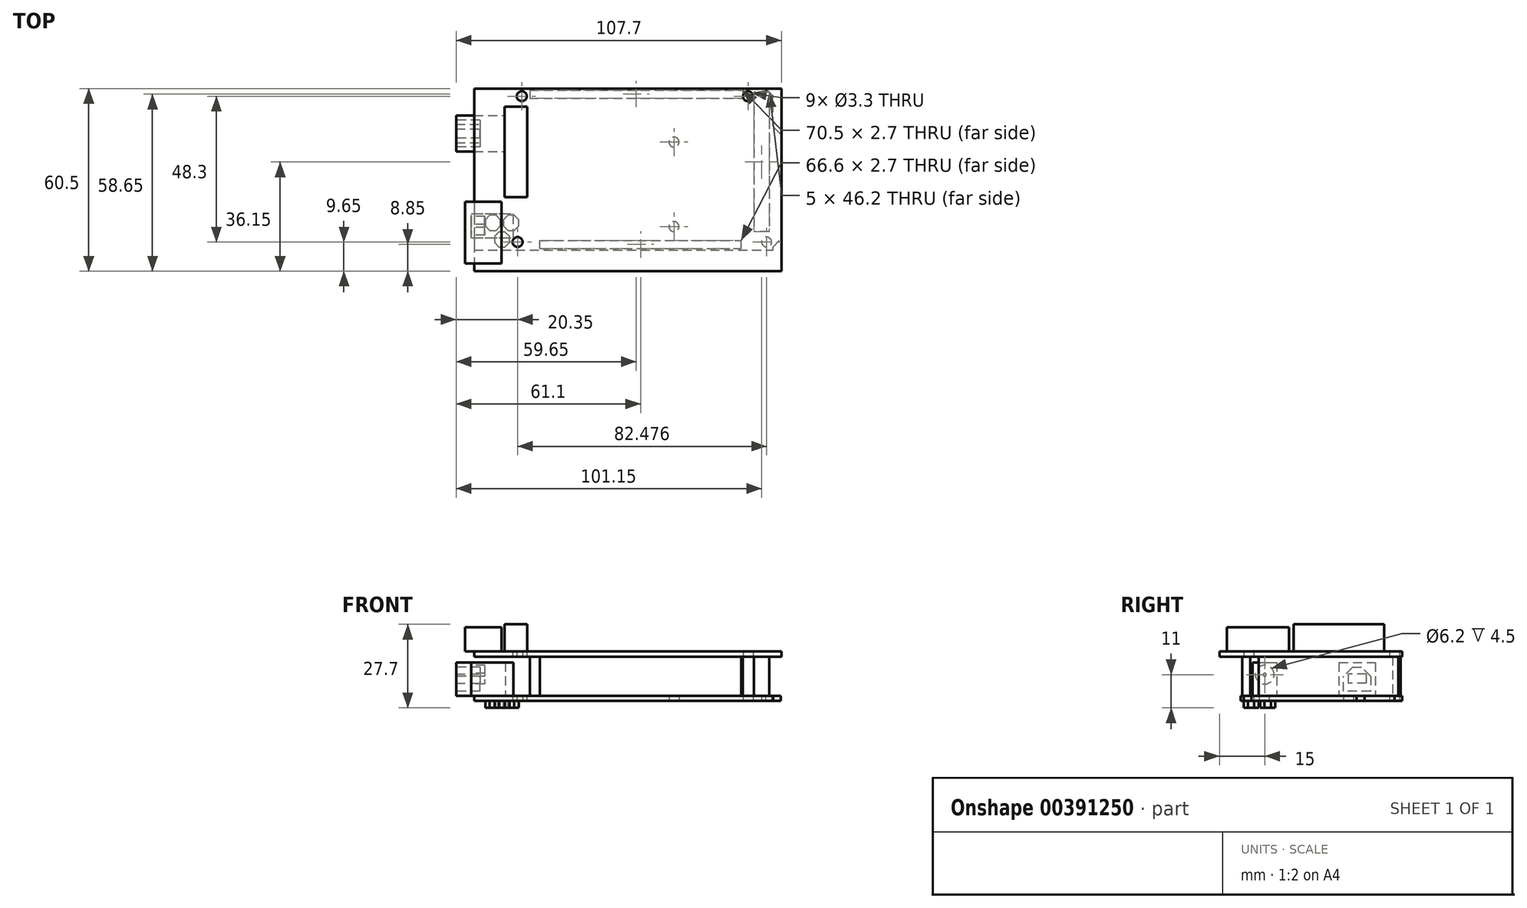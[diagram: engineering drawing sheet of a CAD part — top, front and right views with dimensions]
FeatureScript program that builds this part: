
annotation { "Feature Type Name" : "Feature", "Feature Type Description" : "" }
export const myFeature = defineFeature(function(context is Context, id is Id, definition is map)
    precondition{}
    {
        {
            var Q0;
            Q0=qCreatedBy(makeId("Top.planeOp"),FACE);
            var sketch = newSketch(context, id + "F0", { "sketchPlane" : qUnion([Q0])});
            skLineSegment(sketch, "E0.bottom", {"start": v(0, 0) * mm, "end": v(96.4, 0) * mm});
            skLineSegment(sketch, "E0.top", {"start": v(0, -53.5) * mm, "end": v(98.9, -53.5) * mm});
            skLineSegment(sketch, "E0.left", {"start": v(0, 0) * mm, "end": v(0, -53.5) * mm});
            skLineSegment(sketch, "E0.right", {"start": v(101.5, -15.1) * mm, "end": v(101.5, -49.9) * mm});
            skLineSegment(sketch, "E1", {"start": v(98.9, -53.5) * mm, "end": v(98.9, -52.5) * mm});
            skLineSegment(sketch, "E2", {"start": v(101.5, -15.1) * mm, "end": v(98.9, -12.5) * mm});
            skLineSegment(sketch, "E3", {"start": v(98.9, -52.5) * mm, "end": v(101.5, -49.9) * mm});
            skLineSegment(sketch, "E4", {"start": v(98.9, -2.5) * mm, "end": v(96.4, 0) * mm});
            skLineSegment(sketch, "E5.trimOffspring", {"start": v(98.9, -12.5) * mm, "end": v(98.9, -2.5) * mm});
            skPoint(sketch, "E6.orphan", {"position": v(98.9, 0) * mm});
            skLineSegment(sketch, "E7.bottom", {"start": v(0, -49.5) * mm, "end": v(-1, -49.5) * mm});
            skLineSegment(sketch, "E7.top", {"start": v(0, -40.5) * mm, "end": v(-1, -40.5) * mm});
            skLineSegment(sketch, "E7.left", {"start": v(0, -49.5) * mm, "end": v(0, -40.5) * mm});
            skLineSegment(sketch, "E7.right", {"start": v(-1, -49.5) * mm, "end": v(-1, -40.5) * mm});
            skLineSegment(sketch, "E8.bottom", {"start": v(0, -20.9) * mm, "end": v(-6, -20.9) * mm});
            skLineSegment(sketch, "E8.top", {"start": v(0, -8.9) * mm, "end": v(-6, -8.9) * mm});
            skLineSegment(sketch, "E8.left", {"start": v(0, -20.9) * mm, "end": v(0, -8.9) * mm});
            skLineSegment(sketch, "E8.right", {"start": v(-6, -20.9) * mm, "end": v(-6, -8.9) * mm});
            skCircle(sketch, "E9", {"center": v(15.75, -2.55) * mm, "radius": 1.65 * mm});
            skCircle(sketch, "E10", {"center": v(14.35, -50.85) * mm, "radius": 1.65 * mm});
            skCircle(sketch, "E11", {"center": v(66.15, -45.75) * mm, "radius": 1.65 * mm});
            skCircle(sketch, "E12", {"center": v(66.15, -17.75) * mm, "radius": 1.65 * mm});
            skCircle(sketch, "E13", {"center": v(96.83, -50.85) * mm, "radius": 1.65 * mm});
            skCircle(sketch, "E14", {"center": v(90.65, -2.55) * mm, "radius": 1.65 * mm});
            skLineSegment(sketch, "E15", {"start": v(15.75, -2.55) * mm, "end": v(90.65, -2.55) * mm, "construction": true});
            skLineSegment(sketch, "E16", {"start": v(14.35, -50.85) * mm, "end": v(96.83, -50.85) * mm, "construction": true});
            skLineSegment(sketch, "E17", {"start": v(66.15, -45.75) * mm, "end": v(66.15, -17.75) * mm, "construction": true});
            skSolve(sketch);
        }
        {
            var Q0;
            {var subQ3=sQuery(id+"F0.wireOp",EDGE,"E0.bottom");Q0=makeQuery(id+"F0.imprint","IMPRINT",FACE,{"disambiguationData":[TD([[makeQuery(id+"F0.imprint","IMPRINT",EDGE,{"derivedFrom":subQ3}),-1.0]])]});}
            extrude(context, id + "F1", {"entities" : qUnion([Q0]), "depth" : 1.7 * mm});
        }
        {
            var Q0;
            Q0=makeQuery(id+"F1.opExtrude","CAP_FACE",FACE,{"disambiguationData":[OSD([sQuery(id+"F0.wireOp",EDGE,"E0.bottom"),sQuery(id+"F0.wireOp",EDGE,"E0.top"),sQuery(id+"F0.wireOp",EDGE,"E0.left"),sQuery(id+"F0.wireOp",EDGE,"E0.right"),sQuery(id+"F0.wireOp",EDGE,"E1"),sQuery(id+"F0.wireOp",EDGE,"E2"),sQuery(id+"F0.wireOp",EDGE,"E3"),sQuery(id+"F0.wireOp",EDGE,"E4"),sQuery(id+"F0.wireOp",EDGE,"E5.trimOffspring"),sQuery(id+"F0.wireOp",EDGE,"E7.left"),sQuery(id+"F0.wireOp",EDGE,"E8.left"),sQuery(id+"F0.wireOp",EDGE,"E9"),sQuery(id+"F0.wireOp",EDGE,"E10"),sQuery(id+"F0.wireOp",EDGE,"E11"),sQuery(id+"F0.wireOp",EDGE,"E12"),sQuery(id+"F0.wireOp",EDGE,"E13"),sQuery(id+"F0.wireOp",EDGE,"E14")])],"isStart":true});
            var sketch = newSketch(context, id + "F2", { "sketchPlane" : qUnion([Q0])});
            skCircle(sketch, "E18.cCircle", {"center": v(9.2, 50) * mm, "radius": 2.5 * mm, "construction": true});
            skLineSegment(sketch, "E18.0", {"start": v(8.16, 52.5) * mm, "end": v(10.24, 52.5) * mm});
            skLineSegment(sketch, "E18.1", {"start": v(10.24, 52.5) * mm, "end": v(11.7, 51.04) * mm});
            skLineSegment(sketch, "E18.2", {"start": v(11.7, 51.04) * mm, "end": v(11.7, 48.96) * mm});
            skLineSegment(sketch, "E18.3", {"start": v(11.7, 48.96) * mm, "end": v(10.24, 47.5) * mm});
            skLineSegment(sketch, "E18.4", {"start": v(10.24, 47.5) * mm, "end": v(8.16, 47.5) * mm});
            skLineSegment(sketch, "E18.5", {"start": v(8.16, 47.5) * mm, "end": v(6.7, 48.96) * mm});
            skLineSegment(sketch, "E18.6", {"start": v(6.7, 48.96) * mm, "end": v(6.7, 51.04) * mm});
            skLineSegment(sketch, "E18.7", {"start": v(6.7, 51.04) * mm, "end": v(8.16, 52.5) * mm});
            skPoint(sketch, "E18.0.midPoint", {"position": v(9.2, 52.5) * mm});
            skCircle(sketch, "E19.cCircle", {"center": v(6.2, 44.51) * mm, "radius": 2.5 * mm, "construction": true});
            skLineSegment(sketch, "E19.0", {"start": v(5.16, 47.01) * mm, "end": v(7.24, 47.01) * mm});
            skLineSegment(sketch, "E19.1", {"start": v(7.24, 47.01) * mm, "end": v(8.7, 45.55) * mm});
            skLineSegment(sketch, "E19.2", {"start": v(8.7, 45.55) * mm, "end": v(8.7, 43.48) * mm});
            skLineSegment(sketch, "E19.3", {"start": v(8.7, 43.48) * mm, "end": v(7.24, 42.01) * mm});
            skLineSegment(sketch, "E19.4", {"start": v(7.24, 42.01) * mm, "end": v(5.16, 42.01) * mm});
            skLineSegment(sketch, "E19.5", {"start": v(5.16, 42.01) * mm, "end": v(3.7, 43.48) * mm});
            skLineSegment(sketch, "E19.6", {"start": v(3.7, 43.48) * mm, "end": v(3.7, 45.55) * mm});
            skLineSegment(sketch, "E19.7", {"start": v(3.7, 45.55) * mm, "end": v(5.16, 47.01) * mm});
            skPoint(sketch, "E19.0.midPoint", {"position": v(6.2, 47.01) * mm});
            skCircle(sketch, "E20.cCircle", {"center": v(12.2, 44.51) * mm, "radius": 2.5 * mm, "construction": true});
            skLineSegment(sketch, "E20.0", {"start": v(11.16, 47.01) * mm, "end": v(13.24, 47.01) * mm});
            skLineSegment(sketch, "E20.1", {"start": v(13.24, 47.01) * mm, "end": v(14.7, 45.55) * mm});
            skLineSegment(sketch, "E20.2", {"start": v(14.7, 45.55) * mm, "end": v(14.7, 43.48) * mm});
            skLineSegment(sketch, "E20.3", {"start": v(14.7, 43.48) * mm, "end": v(13.24, 42.01) * mm});
            skLineSegment(sketch, "E20.4", {"start": v(13.24, 42.01) * mm, "end": v(11.16, 42.01) * mm});
            skLineSegment(sketch, "E20.5", {"start": v(11.16, 42.01) * mm, "end": v(9.7, 43.48) * mm});
            skLineSegment(sketch, "E20.6", {"start": v(9.7, 43.48) * mm, "end": v(9.7, 45.55) * mm});
            skLineSegment(sketch, "E20.7", {"start": v(9.7, 45.55) * mm, "end": v(11.16, 47.01) * mm});
            skPoint(sketch, "E20.0.midPoint", {"position": v(12.2, 47.01) * mm});
            skSolve(sketch);
        }
        {
            var Q0;
            Q0 = qSketchRegion(id + "F2", true);
            extrude(context, id + "F3", {"entities" : qUnion([Q0]), "operationType" : NewBodyOperationType.ADD, "depth" : 2.3 * mm});
        }
        {
            var Q0;
            Q0=makeQuery(id+"F1.opExtrude","CAP_FACE",FACE,{"disambiguationData":[OSD([sQuery(id+"F0.wireOp",EDGE,"E0.bottom"),sQuery(id+"F0.wireOp",EDGE,"E0.top"),sQuery(id+"F0.wireOp",EDGE,"E0.left"),sQuery(id+"F0.wireOp",EDGE,"E0.right"),sQuery(id+"F0.wireOp",EDGE,"E1"),sQuery(id+"F0.wireOp",EDGE,"E2"),sQuery(id+"F0.wireOp",EDGE,"E3"),sQuery(id+"F0.wireOp",EDGE,"E4"),sQuery(id+"F0.wireOp",EDGE,"E5.trimOffspring"),sQuery(id+"F0.wireOp",EDGE,"E7.left"),sQuery(id+"F0.wireOp",EDGE,"E8.left"),sQuery(id+"F0.wireOp",EDGE,"E9"),sQuery(id+"F0.wireOp",EDGE,"E10"),sQuery(id+"F0.wireOp",EDGE,"E11"),sQuery(id+"F0.wireOp",EDGE,"E12"),sQuery(id+"F0.wireOp",EDGE,"E13"),sQuery(id+"F0.wireOp",EDGE,"E14")])],"isStart":false});
            var sketch = newSketch(context, id + "F4", { "sketchPlane" : qUnion([Q0])});
            skLineSegment(sketch, "E21.0.0", {"start": v(0, 0) * mm, "end": v(0, -53.5) * mm, "construction": true});
            skLineSegment(sketch, "E21.0.1", {"start": v(0, -53.5) * mm, "end": v(98.9, -53.5) * mm, "construction": true});
            skLineSegment(sketch, "E21.0.2", {"start": v(98.9, -53.5) * mm, "end": v(98.9, -52.5) * mm, "construction": true});
            skLineSegment(sketch, "E21.0.3", {"start": v(98.9, -52.5) * mm, "end": v(101.5, -49.9) * mm, "construction": true});
            skLineSegment(sketch, "E21.0.4", {"start": v(101.5, -49.9) * mm, "end": v(101.5, -15.1) * mm, "construction": true});
            skLineSegment(sketch, "E21.0.5", {"start": v(101.5, -15.1) * mm, "end": v(98.9, -12.5) * mm, "construction": true});
            skLineSegment(sketch, "E21.0.6", {"start": v(98.9, -12.5) * mm, "end": v(98.9, -2.5) * mm, "construction": true});
            skLineSegment(sketch, "E21.0.7", {"start": v(98.9, -2.5) * mm, "end": v(96.4, 0) * mm, "construction": true});
            skLineSegment(sketch, "E21.0.8", {"start": v(96.4, 0) * mm, "end": v(0, 0) * mm, "construction": true});
            skLineSegment(sketch, "E22.bottom", {"start": v(-1, -49.5) * mm, "end": v(13, -49.5) * mm});
            skLineSegment(sketch, "E22.top", {"start": v(-1, -41.5) * mm, "end": v(13, -41.5) * mm});
            skLineSegment(sketch, "E22.left", {"start": v(-1, -49.5) * mm, "end": v(-1, -41.5) * mm});
            skLineSegment(sketch, "E22.right", {"start": v(13, -49.5) * mm, "end": v(13, -41.5) * mm});
            skLineSegment(sketch, "E23.bottom", {"start": v(-6, -20.9) * mm, "end": v(10.3, -20.9) * mm});
            skLineSegment(sketch, "E23.top", {"start": v(-6, -8.9) * mm, "end": v(10.3, -8.9) * mm});
            skLineSegment(sketch, "E23.left", {"start": v(-6, -20.9) * mm, "end": v(-6, -8.9) * mm});
            skLineSegment(sketch, "E23.right", {"start": v(10.3, -20.9) * mm, "end": v(10.3, -8.9) * mm});
            skLineSegment(sketch, "E24.bottom", {"start": v(21.8, -53) * mm, "end": v(88.4, -53) * mm});
            skLineSegment(sketch, "E24.top", {"start": v(21.8, -50.3) * mm, "end": v(88.4, -50.3) * mm});
            skLineSegment(sketch, "E24.left", {"start": v(21.8, -53) * mm, "end": v(21.8, -50.3) * mm});
            skLineSegment(sketch, "E24.right", {"start": v(88.4, -53) * mm, "end": v(88.4, -50.3) * mm});
            skLineSegment(sketch, "E25.bottom", {"start": v(18.4, -0.5) * mm, "end": v(88.9, -0.5) * mm});
            skLineSegment(sketch, "E25.top", {"start": v(18.4, -3.2) * mm, "end": v(88.9, -3.2) * mm});
            skLineSegment(sketch, "E25.left", {"start": v(18.4, -0.5) * mm, "end": v(18.4, -3.2) * mm});
            skLineSegment(sketch, "E25.right", {"start": v(88.9, -0.5) * mm, "end": v(88.9, -3.2) * mm});
            skLineSegment(sketch, "E26.bottom", {"start": v(97.65, -1.25) * mm, "end": v(92.65, -1.25) * mm});
            skLineSegment(sketch, "E26.top", {"start": v(97.65, -47.45) * mm, "end": v(92.65, -47.45) * mm});
            skLineSegment(sketch, "E26.left", {"start": v(97.65, -1.25) * mm, "end": v(97.65, -47.45) * mm});
            skLineSegment(sketch, "E26.right", {"start": v(92.65, -1.25) * mm, "end": v(92.65, -47.45) * mm});
            skSolve(sketch);
        }
        {
            var Q0;
            Q0=makeQuery(id+"F4.imprint","IMPRINT",FACE,{"disambiguationData":[TD([[makeQuery(id+"F4.imprint","IMPRINT",EDGE,{"derivedFrom":sQuery(id+"F4.wireOp",EDGE,"E24.bottom")}),1.0]])]});
            var Q1;
            Q1=makeQuery(id+"F4.imprint","IMPRINT",FACE,{"disambiguationData":[TD([[makeQuery(id+"F4.imprint","IMPRINT",EDGE,{"derivedFrom":sQuery(id+"F4.wireOp",EDGE,"E25.bottom")}),-1.0]])]});
            var Q2;
            Q2=makeQuery(id+"F4.imprint","IMPRINT",FACE,{"disambiguationData":[TD([[makeQuery(id+"F4.imprint","IMPRINT",EDGE,{"derivedFrom":sQuery(id+"F4.wireOp",EDGE,"E26.bottom")}),1.0]])]});
            extrude(context, id + "F5", {"entities" : qUnion([Q0, Q1, Q2]), "operationType" : NewBodyOperationType.ADD, "depth" : 13 * mm});
        }
        {
            var Q0;
            {var subQ0=sQuery(id+"F4.wireOp",EDGE,"E23.right");Q0=makeQuery(id+"F4.imprint","IMPRINT",FACE,{"disambiguationData":[TD([[makeQuery(id+"F4.imprint","IMPRINT",EDGE,{"derivedFrom":subQ0}),1.0]])]});}
            var Q1;
            {var subQ0=sQuery(id+"F4.wireOp",EDGE,"E23.left");Q1=makeQuery(id+"F4.imprint","IMPRINT",FACE,{"disambiguationData":[TD([[makeQuery(id+"F4.imprint","IMPRINT",EDGE,{"derivedFrom":subQ0}),-1.0]])]});}
            extrude(context, id + "F6", {"entities" : qUnion([Q0, Q1]), "operationType" : NewBodyOperationType.ADD, "depth" : 11 * mm});
        }
        {
            var Q0;
            {var subQ0=sQuery(id+"F4.wireOp",EDGE,"E22.right");Q0=makeQuery(id+"F4.imprint","IMPRINT",FACE,{"disambiguationData":[TD([[makeQuery(id+"F4.imprint","IMPRINT",EDGE,{"derivedFrom":subQ0}),1.0]])]});}
            var Q1;
            {var subQ0=sQuery(id+"F4.wireOp",EDGE,"E22.left");Q1=makeQuery(id+"F4.imprint","IMPRINT",FACE,{"disambiguationData":[TD([[makeQuery(id+"F4.imprint","IMPRINT",EDGE,{"derivedFrom":subQ0}),-1.0]])]});}
            extrude(context, id + "F7", {"entities" : qUnion([Q0, Q1]), "operationType" : NewBodyOperationType.ADD, "depth" : 11 * mm});
        }
        {
            var Q0;
            Q0=makeQuery(id+"F6.opExtrude","SWEPT_FACE",FACE,{"disambiguationData":[OSD([sQuery(id+"F4.wireOp",EDGE,"E23.left")])]});
            var sketch = newSketch(context, id + "F8", { "sketchPlane" : qUnion([Q0])});
            skLineSegment(sketch, "E27.0", {"start": v(10.4, 3.2) * mm, "end": v(19.4, 3.2) * mm});
            skLineSegment(sketch, "E27.1", {"start": v(10.4, 11.2) * mm, "end": v(10.4, 3.2) * mm});
            skLineSegment(sketch, "E27.2", {"start": v(19.4, 11.2) * mm, "end": v(10.4, 11.2) * mm});
            skLineSegment(sketch, "E27.3", {"start": v(19.4, 3.2) * mm, "end": v(19.4, 11.2) * mm});
            skSolve(sketch);
        }
        {
            var Q0;
            Q0=makeQuery(id+"F8.imprint","IMPRINT",FACE,{"disambiguationData":[TD([[makeQuery(id+"F8.imprint","IMPRINT",EDGE,{"derivedFrom":sQuery(id+"F8.wireOp",EDGE,"E27.0")}),1.0]])]});
            extrude(context, id + "F9", {"entities" : qUnion([Q0]), "operationType" : NewBodyOperationType.REMOVE, "oppositeDirection" : true, "depth" : 7.9 * mm});
        }
        {
            var Q0;
            Q0=makeQuery(id+"F7.opExtrude","SWEPT_FACE",FACE,{"disambiguationData":[OSD([sQuery(id+"F4.wireOp",EDGE,"E22.left")])]});
            var sketch = newSketch(context, id + "F10", { "sketchPlane" : qUnion([Q0])});
            skCircle(sketch, "E28", {"center": v(45.5, 8.7) * mm, "radius": 3.1 * mm});
            skLineSegment(sketch, "E29", {"start": v(42.4, 8.7) * mm, "end": v(41.5, 8.7) * mm, "construction": true});
            skLineSegment(sketch, "E30", {"start": v(48.6, 8.7) * mm, "end": v(49.5, 8.7) * mm, "construction": true});
            skLineSegment(sketch, "E31", {"start": v(45.5, 11.8) * mm, "end": v(45.5, 12.7) * mm, "construction": true});
            skCircle(sketch, "E32", {"center": v(45.5, 8.7) * mm, "radius": 0.5 * mm});
            skSolve(sketch);
        }
        {
            var Q0;
            Q0 = qSketchRegion(id + "F10", true);
            extrude(context, id + "F11", {"entities" : qUnion([Q0]), "operationType" : NewBodyOperationType.REMOVE, "oppositeDirection" : true, "depth" : 4.5 * mm});
        }
        {
            var Q0;
            Q0=makeQuery(id+"F9.boolean.opBoolean","COPY",EDGE,{"derivedFrom":makeQuery(id+"F9.opExtrude","SWEPT_EDGE",EDGE,{"disambiguationData":[OSD([sQuery(id+"F8.wireOp",EDGE,"E27.1"),sQuery(id+"F8.wireOp",EDGE,"E27.2")])]})});
            var Q1;
            Q1=makeQuery(id+"F9.boolean.opBoolean","COPY",EDGE,{"derivedFrom":makeQuery(id+"F9.opExtrude","SWEPT_EDGE",EDGE,{"disambiguationData":[OSD([sQuery(id+"F8.wireOp",EDGE,"E27.2"),sQuery(id+"F8.wireOp",EDGE,"E27.3")])]})});
            chamfer(context, id + "F12", {"entities" : qUnion([Q0, Q1]), "width" : 3 * mm, "tangentPropagation" : true});
        }
        {
            var Q0;
            Q0=makeQuery(id+"F9.boolean.opBoolean","COPY",FACE,{"derivedFrom":makeQuery(id+"F9.opExtrude","CAP_FACE",FACE,{"disambiguationData":[OSD([sQuery(id+"F8.wireOp",EDGE,"E27.0"),sQuery(id+"F8.wireOp",EDGE,"E27.1"),sQuery(id+"F8.wireOp",EDGE,"E27.2"),sQuery(id+"F8.wireOp",EDGE,"E27.3")])],"isStart":false})});
            var sketch = newSketch(context, id + "F13", { "sketchPlane" : qUnion([Q0])});
            skLineSegment(sketch, "E33.bottom", {"start": v(11.9, 8.9) * mm, "end": v(17.9, 8.9) * mm});
            skLineSegment(sketch, "E33.top", {"start": v(11.9, 5.9) * mm, "end": v(17.9, 5.9) * mm});
            skLineSegment(sketch, "E33.left", {"start": v(11.9, 8.9) * mm, "end": v(11.9, 5.9) * mm});
            skLineSegment(sketch, "E33.right", {"start": v(17.9, 8.9) * mm, "end": v(17.9, 5.9) * mm});
            skLineSegment(sketch, "E34", {"start": v(11.9, 6.28) * mm, "end": v(10.4, 6.28) * mm, "construction": true});
            skLineSegment(sketch, "E35", {"start": v(17.9, 7.71) * mm, "end": v(19.4, 7.71) * mm, "construction": true});
            skLineSegment(sketch, "E36", {"start": v(14.9, 11.2) * mm, "end": v(14.9, 8.9) * mm, "construction": true});
            skSolve(sketch);
        }
        {
            var Q0;
            Q0=makeQuery(id+"F13.imprint","IMPRINT",FACE,{"disambiguationData":[TD([[makeQuery(id+"F13.imprint","IMPRINT",EDGE,{"derivedFrom":sQuery(id+"F13.wireOp",EDGE,"E33.bottom")}),-1.0]])]});
            var Q1;
            Q1=makeQuery(id+"F6.opExtrude","SWEPT_FACE",FACE,{"disambiguationData":[OSD([sQuery(id+"F4.wireOp",EDGE,"E23.left")])]});
            extrude(context, id + "F14", {"entities" : qUnion([Q0]), "operationType" : NewBodyOperationType.ADD, "endBound" : BoundingType.UP_TO_SURFACE, "endBoundEntityFace" : qUnion([Q1]), "depth" : 25 * mm});
        }
        {
            var Q0;
            Q0=makeQuery(id+"F5.opExtrude","CAP_FACE",FACE,{"disambiguationData":[OSD([sQuery(id+"F4.wireOp",EDGE,"E25.bottom"),sQuery(id+"F4.wireOp",EDGE,"E25.top"),sQuery(id+"F4.wireOp",EDGE,"E25.left"),sQuery(id+"F4.wireOp",EDGE,"E25.right")])],"isStart":false});
            cPlane(context, id + "F15", {"entities" : qUnion([Q0]), "cplaneType" : CPlaneType.OFFSET, "offset" : 0 * mm, "width" : 150 * mm, "height" : 150 * mm});
        }
        {
            var Q0;
            Q0=qCreatedBy(id+"F15.planeOp",FACE);
            var sketch = newSketch(context, id + "F16", { "sketchPlane" : qUnion([Q0])});
            skLineSegment(sketch, "E37.bottom", {"start": v(0, 0) * mm, "end": v(101.7, 0) * mm});
            skLineSegment(sketch, "E37.top", {"start": v(0, -60.5) * mm, "end": v(101.7, -60.5) * mm});
            skLineSegment(sketch, "E37.left", {"start": v(0, 0) * mm, "end": v(0, -60.5) * mm});
            skLineSegment(sketch, "E37.right", {"start": v(101.7, 0) * mm, "end": v(101.7, -60.5) * mm});
            skCircle(sketch, "E38.0", {"center": v(15.75, -2.55) * mm, "radius": 1.65 * mm});
            skCircle(sketch, "E39.0", {"center": v(14.35, -50.85) * mm, "radius": 1.65 * mm});
            skCircle(sketch, "E40.0", {"center": v(90.65, -2.55) * mm, "radius": 1.65 * mm});
            skSolve(sketch);
        }
        {
            var Q0;
            Q0=makeQuery(id+"F16.imprint","IMPRINT",FACE,{"disambiguationData":[TD([[makeQuery(id+"F16.imprint","IMPRINT",EDGE,{"derivedFrom":sQuery(id+"F16.wireOp",EDGE,"E37.bottom")}),-1.0]])]});
            extrude(context, id + "F17", {"entities" : qUnion([Q0]), "operationType" : NewBodyOperationType.ADD, "depth" : 1.7 * mm});
        }
        {
            var Q0;
            Q0=makeQuery(id+"F17.opExtrude","CAP_FACE",FACE,{"disambiguationData":[OSD([sQuery(id+"F16.wireOp",EDGE,"E37.bottom"),sQuery(id+"F16.wireOp",EDGE,"E37.top"),sQuery(id+"F16.wireOp",EDGE,"E37.left"),sQuery(id+"F16.wireOp",EDGE,"E37.right"),sQuery(id+"F16.wireOp",EDGE,"E38.0"),sQuery(id+"F16.wireOp",EDGE,"E39.0"),sQuery(id+"F16.wireOp",EDGE,"E40.0")])],"isStart":false});
            var sketch = newSketch(context, id + "F18", { "sketchPlane" : qUnion([Q0])});
            skLineSegment(sketch, "E41.bottom", {"start": v(10, -6) * mm, "end": v(17.5, -6) * mm});
            skLineSegment(sketch, "E41.top", {"start": v(10, -36) * mm, "end": v(17.5, -36) * mm});
            skLineSegment(sketch, "E41.left", {"start": v(10, -6) * mm, "end": v(10, -36) * mm});
            skLineSegment(sketch, "E41.right", {"start": v(17.5, -6) * mm, "end": v(17.5, -36) * mm});
            skLineSegment(sketch, "E42.bottom", {"start": v(9, -58) * mm, "end": v(-3, -58) * mm});
            skLineSegment(sketch, "E42.top", {"start": v(9, -37.5) * mm, "end": v(-3, -37.5) * mm});
            skLineSegment(sketch, "E42.left", {"start": v(9, -58) * mm, "end": v(9, -37.5) * mm});
            skLineSegment(sketch, "E42.right", {"start": v(-3, -58) * mm, "end": v(-3, -37.5) * mm});
            skSolve(sketch);
        }
        {
            var Q0;
            Q0=makeQuery(id+"F18.imprint","IMPRINT",FACE,{"disambiguationData":[TD([[makeQuery(id+"F18.imprint","IMPRINT",EDGE,{"derivedFrom":sQuery(id+"F18.wireOp",EDGE,"E41.bottom")}),-1.0]])]});
            extrude(context, id + "F19", {"entities" : qUnion([Q0]), "operationType" : NewBodyOperationType.ADD, "depth" : 9 * mm});
        }
        {
            var Q0;
            {var subQ0=sQuery(id+"F18.wireOp",EDGE,"E42.left");Q0=makeQuery(id+"F18.imprint","IMPRINT",FACE,{"disambiguationData":[TD([[makeQuery(id+"F18.imprint","IMPRINT",EDGE,{"derivedFrom":subQ0}),1.0]])]});}
            var Q1;
            {var subQ0=sQuery(id+"F18.wireOp",EDGE,"E42.right");Q1=makeQuery(id+"F18.imprint","IMPRINT",FACE,{"disambiguationData":[TD([[makeQuery(id+"F18.imprint","IMPRINT",EDGE,{"derivedFrom":subQ0}),-1.0]])]});}
            extrude(context, id + "F20", {"entities" : qUnion([Q0, Q1]), "operationType" : NewBodyOperationType.ADD, "depth" : 8 * mm});
        }
    });
